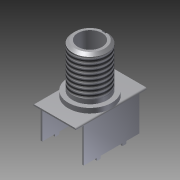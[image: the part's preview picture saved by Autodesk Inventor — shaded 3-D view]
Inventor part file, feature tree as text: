
AUTODESK INVENTOR PART (.ipt)
format: ipt  version: 2014 (Build 180170000, 170)  size: 195,072 bytes
history: native  units: in
note: dims shown in document units (in); Inventor stores cm internally (conversion verified against a paired STEP export)
features: other x35, sketch x5, extrude x3, revolve x1, thread x1, hole x1
ambient origin geometry x8: Origin, YZ Plane, XZ Plane, XY Plane, X Axis, Y Axis, Z Axis, Center Point
bodies: Solid1 (feature_tree)
feature tree (46):
  extrude  "Extrusion1"  Depth=0.311in TaperAngle=0.0deg
  extrude  "Extrusion2"  Depth=0.285in
  revolve  "Revolution1"  [1 undecoded]
  thread  "Thread1"  [1 undecoded]
  extrude  "Extrusion3"  [1 undecoded]
  hole  "Drilling 1"  [1 undecoded]
  other  "1_XY"
  other  "1_YZ"
  other  "1_ZX"
  other  "1_X"
  other  "1_Y"
  other  "1_Z"
  other  "1_Center"
  other  "2_XY"
  other  "2_YZ"
  other  "2_ZX"
  other  "2_X"
  other  "2_Y"
  other  "2_Z"
  other  "2_Center"
  other  "3_XY"
  other  "3_YZ"
  other  "3_ZX"
  other  "3_X"
  other  "3_Y"
  other  "3_Z"
  other  "3_Center"
  other  "4_XY"
  other  "4_YZ"
  other  "4_ZX"
  other  "4_X"
  other  "4_Y"
  other  "4_Z"
  other  "4_Center"
  other  "to_base_XY"
  other  "to_base_YZ"
  other  "to_base_ZX"
  other  "to_base_X"
  other  "to_base_Y"
  other  "to_base_Z"
  other  "to_base_Center"
  sketch  "Sketch_1"  dims[d0=0.512in d1=0.0in d2=0.311in d3=0.0in]
  sketch  "Sketch_2"  dims[d4=360.0deg d5=0.285in d6=0.03in]
  sketch  "Sketch_15"
  sketch  "Sketch_8"  dims[d9=0.175in d10=0.75in d11=0.375in d12=0.25in d13=0.5635in d14=0.36in d15=0.0in]
  sketch  "Sketch5"  dims[d7=0.385in d8=0.0in]
note: 4 required parameter values undecoded (feature->parameter linkage not recoverable at this tier; creation-order binding heuristic only, values carry confidence <= 0.55)
